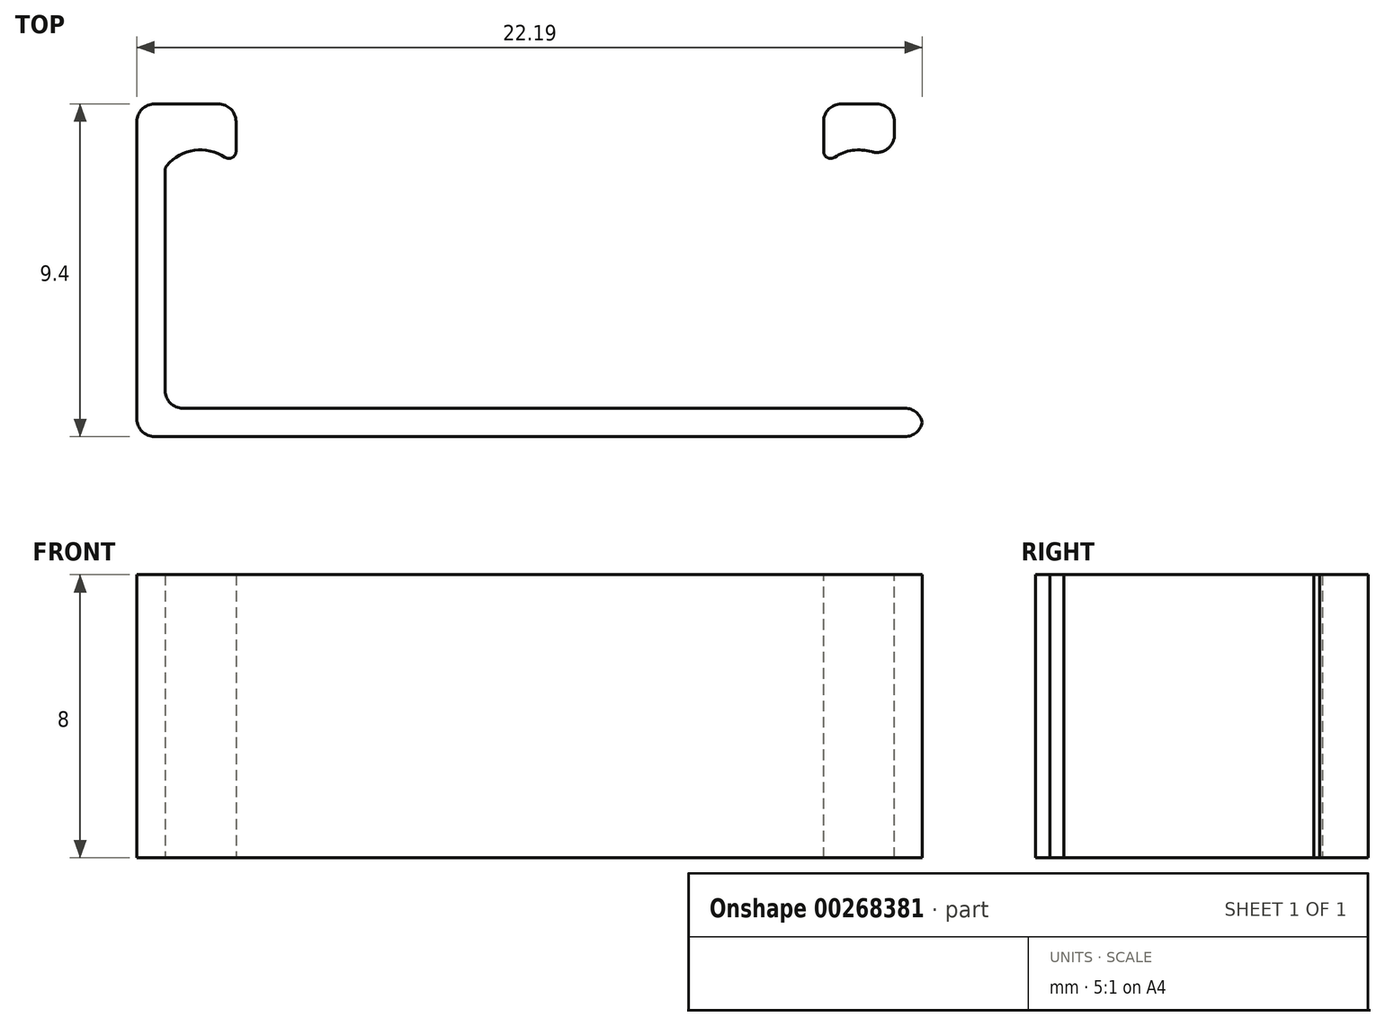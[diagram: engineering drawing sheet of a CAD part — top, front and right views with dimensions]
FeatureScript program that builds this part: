
annotation { "Feature Type Name" : "Feature", "Feature Type Description" : "" }
export const myFeature = defineFeature(function(context is Context, id is Id, definition is map)
    precondition{}
    {
        {
            var Q0;
            Q0=qCreatedBy(makeId("Top.planeOp"),FACE);
            var sketch = newSketch(context, id + "F0", { "sketchPlane" : qUnion([Q0])});
            skLineSegment(sketch, "E0.bottom", {"start": v(0, 0) * mm, "end": v(0.8, 0) * mm});
            skLineSegment(sketch, "E0.top", {"start": v(0, 8.6) * mm, "end": v(0.8, 8.6) * mm});
            skLineSegment(sketch, "E0.left", {"start": v(0, 0) * mm, "end": v(0, 8.6) * mm});
            skLineSegment(sketch, "E0.right", {"start": v(0.8, 0) * mm, "end": v(0.8, 8.6) * mm});
            skLineSegment(sketch, "E1.bottom", {"start": v(0, 0) * mm, "end": v(22.2, 0) * mm});
            skLineSegment(sketch, "E1.top", {"start": v(0, -0.8) * mm, "end": v(22.2, -0.8) * mm});
            skLineSegment(sketch, "E1.left", {"start": v(0, 0) * mm, "end": v(0, -0.8) * mm});
            skLineSegment(sketch, "E1.right", {"start": v(22.2, 0) * mm, "end": v(22.2, -0.8) * mm});
            skLineSegment(sketch, "E2.bottom", {"start": v(22.2, 0) * mm, "end": v(21.4, 0) * mm});
            skLineSegment(sketch, "E2.top", {"start": v(22.2, 8.6) * mm, "end": v(21.4, 8.6) * mm});
            skLineSegment(sketch, "E2.left", {"start": v(22.2, 0) * mm, "end": v(22.2, 8.6) * mm});
            skLineSegment(sketch, "E2.right", {"start": v(21.4, 0) * mm, "end": v(21.4, 8.6) * mm});
            skLineSegment(sketch, "E3.bottom", {"start": v(0.8, 8.6) * mm, "end": v(2.8, 8.6) * mm});
            skLineSegment(sketch, "E3.top", {"start": v(0.8, 6.8) * mm, "end": v(2.8, 6.8) * mm});
            skLineSegment(sketch, "E3.left", {"start": v(0.8, 8.6) * mm, "end": v(0.8, 6.8) * mm});
            skLineSegment(sketch, "E3.right", {"start": v(2.8, 8.6) * mm, "end": v(2.8, 6.8) * mm});
            skLineSegment(sketch, "E4.bottom", {"start": v(21.4, 8.6) * mm, "end": v(19.4, 8.6) * mm});
            skLineSegment(sketch, "E4.top", {"start": v(21.4, 6.8) * mm, "end": v(19.4, 6.8) * mm});
            skLineSegment(sketch, "E4.left", {"start": v(21.4, 8.6) * mm, "end": v(21.4, 6.8) * mm});
            skLineSegment(sketch, "E4.right", {"start": v(19.4, 8.6) * mm, "end": v(19.4, 6.8) * mm});
            skArc(sketch, "E5", {"start": v(2.8, 6.8) * mm, "mid": v(1.8, 7.3) * mm, "end": v(0.8, 6.8) * mm});
            skArc(sketch, "E6", {"start": v(21.4, 6.8) * mm, "mid": v(20.4, 7.3) * mm, "end": v(19.4, 6.8) * mm});
            skSolve(sketch);
        }
        {
            var Q0;
            Q0=makeQuery(id+"F0.imprint","IMPRINT",FACE,{"disambiguationData":[TD([[makeQuery(id+"F0.imprint","IMPRINT",EDGE,{"derivedFrom":sQuery(id+"F0.wireOp",EDGE,"E0.top")}),-1.0]])]});
            var Q1;
            Q1=makeQuery(id+"F0.imprint","IMPRINT",FACE,{"disambiguationData":[TD([[makeQuery(id+"F0.imprint","IMPRINT",EDGE,{"derivedFrom":sQuery(id+"F0.wireOp",EDGE,"E1.top")}),1.0]])]});
            var Q2;
            Q2=makeQuery(id+"F0.imprint","IMPRINT",FACE,{"disambiguationData":[TD([[makeQuery(id+"F0.imprint","IMPRINT",EDGE,{"derivedFrom":sQuery(id+"F0.wireOp",EDGE,"E2.bottom")}),-1.0]])]});
            var Q3;
            Q3=makeQuery(id+"F0.imprint","IMPRINT",FACE,{"disambiguationData":[TD([[makeQuery(id+"F0.imprint","IMPRINT",EDGE,{"derivedFrom":sQuery(id+"F0.wireOp",EDGE,"E4.bottom")}),1.0]])]});
            var Q4;
            Q4=makeQuery(id+"F0.imprint","IMPRINT",FACE,{"disambiguationData":[TD([[makeQuery(id+"F0.imprint","IMPRINT",EDGE,{"derivedFrom":sQuery(id+"F0.wireOp",EDGE,"E3.bottom")}),-1.0]])]});
            extrude(context, id + "F1", {"entities" : qUnion([Q0, Q1, Q2, Q3, Q4]), "depth" : 8 * mm});
        }
        {
            var Q0;
            Q0=makeQuery(id+"F1.opExtrude","SWEPT_EDGE",EDGE,{"disambiguationData":[OSD([sQuery(id+"F0.wireOp",EDGE,"E1.top"),sQuery(id+"F0.wireOp",EDGE,"E1.right")])]});
            var Q1;
            Q1=makeQuery(id+"F1.opExtrude","SWEPT_EDGE",EDGE,{"disambiguationData":[OSD([sQuery(id+"F0.wireOp",EDGE,"E1.top"),sQuery(id+"F0.wireOp",EDGE,"E1.left")])]});
            var Q2;
            Q2=makeQuery(id+"F1.opExtrude","SWEPT_EDGE",EDGE,{"disambiguationData":[OSD([sQuery(id+"F0.wireOp",EDGE,"E2.top"),sQuery(id+"F0.wireOp",EDGE,"E2.left")])]});
            var Q3;
            Q3=makeQuery(id+"F1.opExtrude","SWEPT_EDGE",EDGE,{"disambiguationData":[OSD([sQuery(id+"F0.wireOp",EDGE,"E4.bottom"),sQuery(id+"F0.wireOp",EDGE,"E4.right")])]});
            var Q4;
            Q4=makeQuery(id+"F1.opExtrude","SWEPT_EDGE",EDGE,{"disambiguationData":[OSD([sQuery(id+"F0.wireOp",EDGE,"E0.top"),sQuery(id+"F0.wireOp",EDGE,"E0.left")])]});
            var Q5;
            Q5=makeQuery(id+"F1.opExtrude","SWEPT_EDGE",EDGE,{"disambiguationData":[OSD([sQuery(id+"F0.wireOp",EDGE,"E3.bottom"),sQuery(id+"F0.wireOp",EDGE,"E3.right")])]});
            var Q6;
            Q6=makeQuery(id+"F1.opExtrude","SWEPT_EDGE",EDGE,{"disambiguationData":[OSD([sQuery(id+"F0.wireOp",EDGE,"E0.right"),sQuery(id+"F0.wireOp",EDGE,"E1.bottom")])]});
            var Q7;
            Q7=makeQuery(id+"F1.opExtrude","SWEPT_EDGE",EDGE,{"disambiguationData":[OSD([sQuery(id+"F0.wireOp",EDGE,"E1.bottom"),sQuery(id+"F0.wireOp",EDGE,"E2.bottom"),sQuery(id+"F0.wireOp",EDGE,"E2.right")])]});
            fillet(context, id + "F2", {"entities" : qUnion([Q0, Q1, Q2, Q3, Q4, Q5, Q6, Q7]), "radius" : 0.5 * mm, "tangentPropagation" : true, "allowEdgeOverflow" : false});
        }
        {
            var Q0;
            Q0=makeQuery(id+"F1.opExtrude","SWEPT_EDGE",EDGE,{"disambiguationData":[OSD([sQuery(id+"F0.wireOp",EDGE,"E3.top"),sQuery(id+"F0.wireOp",EDGE,"E3.right"),sQuery(id+"F0.wireOp",EDGE,"E5")])]});
            var Q1;
            Q1=makeQuery(id+"F1.opExtrude","SWEPT_EDGE",EDGE,{"disambiguationData":[OSD([sQuery(id+"F0.wireOp",EDGE,"E0.right"),sQuery(id+"F0.wireOp",EDGE,"E3.top"),sQuery(id+"F0.wireOp",EDGE,"E3.left"),sQuery(id+"F0.wireOp",EDGE,"E5")])]});
            var Q2;
            Q2=makeQuery(id+"F1.opExtrude","SWEPT_EDGE",EDGE,{"disambiguationData":[OSD([sQuery(id+"F0.wireOp",EDGE,"E4.top"),sQuery(id+"F0.wireOp",EDGE,"E4.right"),sQuery(id+"F0.wireOp",EDGE,"E6")])]});
            var Q3;
            Q3=makeQuery(id+"F1.opExtrude","SWEPT_EDGE",EDGE,{"disambiguationData":[OSD([sQuery(id+"F0.wireOp",EDGE,"E2.right"),sQuery(id+"F0.wireOp",EDGE,"E4.top"),sQuery(id+"F0.wireOp",EDGE,"E4.left"),sQuery(id+"F0.wireOp",EDGE,"E6")])]});
            fillet(context, id + "F3", {"entities" : qUnion([Q0, Q1, Q2, Q3]), "radius" : 0.2 * mm, "tangentPropagation" : true, "allowEdgeOverflow" : false});
        }
    });
